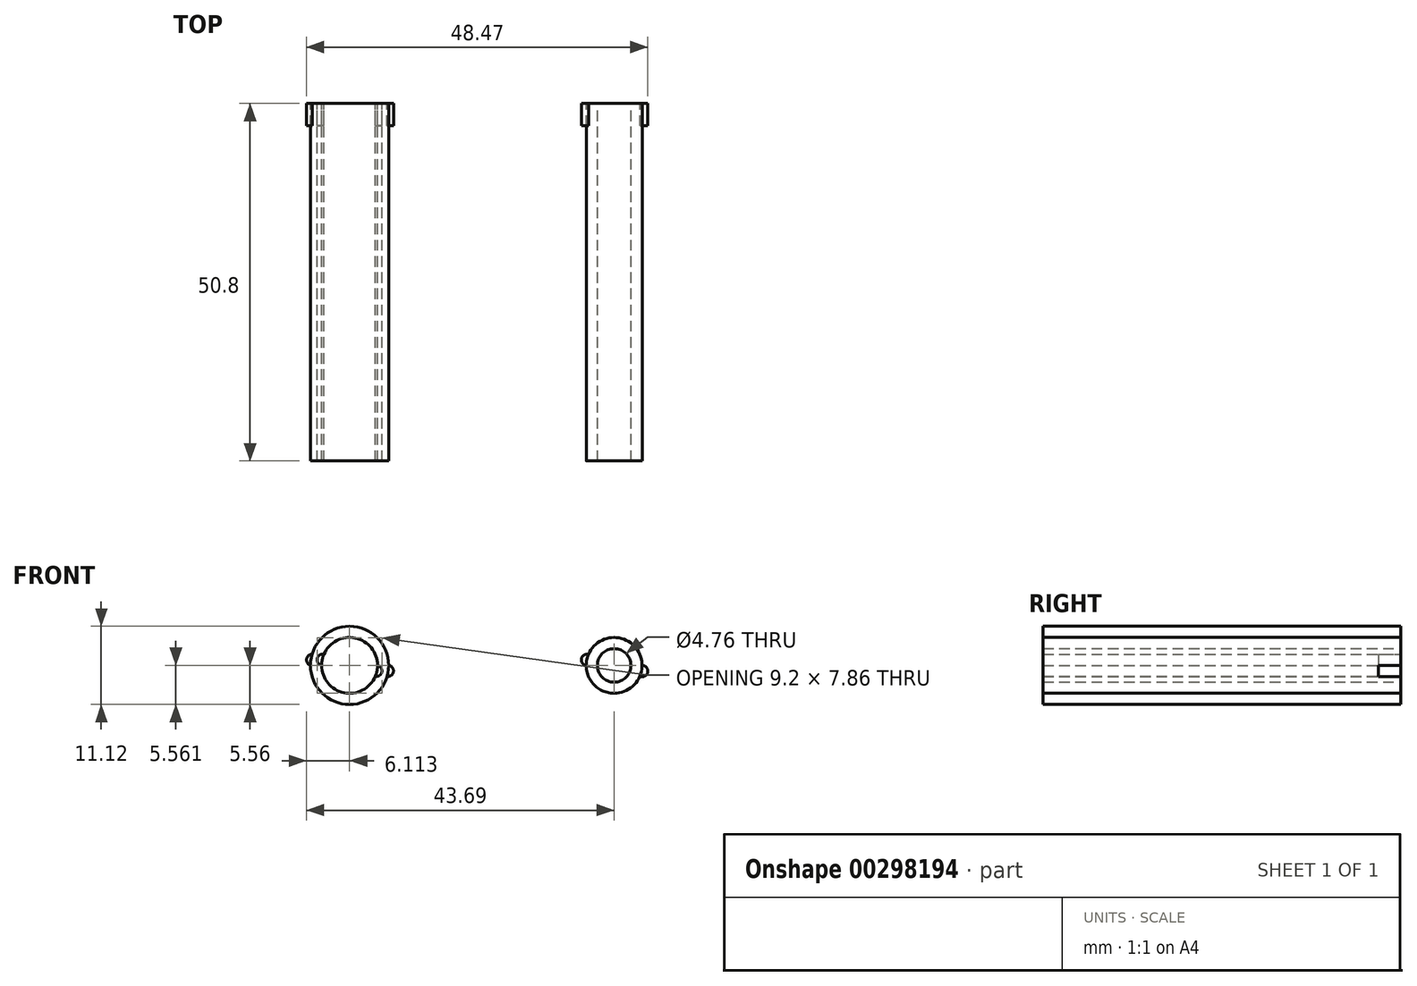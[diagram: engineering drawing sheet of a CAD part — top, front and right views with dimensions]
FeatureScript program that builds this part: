
annotation { "Feature Type Name" : "Feature", "Feature Type Description" : "" }
export const myFeature = defineFeature(function(context is Context, id is Id, definition is map)
    precondition{}
    {
        {
            var Q0;
            Q0=qCreatedBy(makeId("Front.planeOp"),FACE);
            var sketch = newSketch(context, id + "F0", { "sketchPlane" : qUnion([Q0])});
            skCircle(sketch, "E0", {"center": v(46.3, 0) * mm, "radius": 3.97 * mm});
            skCircle(sketch, "E1", {"center": v(8.73, 0) * mm, "radius": 5.56 * mm});
            skCircle(sketch, "E2.0", {"center": v(46.3, 0) * mm, "radius": 2.38 * mm});
            skCircle(sketch, "E3.0", {"center": v(8.73, 0) * mm, "radius": 3.97 * mm});
            skArc(sketch, "E4", {"start": v(3.4, 1.59) * mm, "mid": v(2.62, 0.9) * mm, "end": v(3.18, 0) * mm});
            skArc(sketch, "E5", {"start": v(14.06, -1.57) * mm, "mid": v(14.96, -0.9) * mm, "end": v(14.29, 0) * mm});
            skArc(sketch, "E6", {"start": v(5.1, 1.59) * mm, "mid": v(4.13, 0.96) * mm, "end": v(4.76, 0) * mm});
            skArc(sketch, "E7", {"start": v(12.38, -1.56) * mm, "mid": v(13.32, -0.94) * mm, "end": v(12.7, 0) * mm});
            skArc(sketch, "E8", {"start": v(42.65, 1.56) * mm, "mid": v(41.65, 0.95) * mm, "end": v(42.33, 0) * mm});
            skArc(sketch, "E9", {"start": v(49.95, -1.56) * mm, "mid": v(51.06, -0.97) * mm, "end": v(50.27, 0) * mm});
            skSolve(sketch);
        }
        {
            var Q0;
            Q0=makeQuery(id+"F0.imprint","IMPRINT",FACE,{"disambiguationData":[TD([[makeQuery(id+"F0.imprint","IMPRINT",EDGE,{"derivedFrom":sQuery(id+"F0.wireOp",EDGE,"E2.0")}),-1.0]])]});
            var Q1;
            {var subQ7=sQuery(id+"F0.wireOp",EDGE,"E6");Q1=makeQuery(id+"F0.imprint","IMPRINT",FACE,{"disambiguationData":[TD([[makeQuery(id+"F0.imprint","IMPRINT",EDGE,{"derivedFrom":subQ7}),-1.0]])]});}
            extrude(context, id + "F1", {"entities" : qUnion([Q0, Q1]), "depth" : 50.8 * mm});
        }
        {
            var Q0;
            {var subQ0=sQuery(id+"F0.wireOp",EDGE,"E6");Q0=makeQuery(id+"F0.imprint","IMPRINT",FACE,{"disambiguationData":[TD([[makeQuery(id+"F0.imprint","IMPRINT",EDGE,{"derivedFrom":subQ0}),1.0]])]});}
            var Q1;
            {var subQ0=sQuery(id+"F0.wireOp",EDGE,"E7");Q1=makeQuery(id+"F0.imprint","IMPRINT",FACE,{"disambiguationData":[TD([[makeQuery(id+"F0.imprint","IMPRINT",EDGE,{"derivedFrom":subQ0}),1.0]])]});}
            var Q2;
            {var subQ0=sQuery(id+"F0.wireOp",EDGE,"E5");Q2=makeQuery(id+"F0.imprint","IMPRINT",FACE,{"disambiguationData":[TD([[makeQuery(id+"F0.imprint","IMPRINT",EDGE,{"derivedFrom":subQ0}),1.0]])]});}
            var Q3;
            {var subQ0=sQuery(id+"F0.wireOp",EDGE,"E4");Q3=makeQuery(id+"F0.imprint","IMPRINT",FACE,{"disambiguationData":[TD([[makeQuery(id+"F0.imprint","IMPRINT",EDGE,{"derivedFrom":subQ0}),1.0]])]});}
            var Q4;
            {var subQ0=sQuery(id+"F0.wireOp",EDGE,"P9wS2eRt-gNgB-vEHD-qdaP-UL0ial1GIJOu");Q4=makeQuery(id+"F0.imprint","IMPRINT",FACE,{"disambiguationData":[TD([[makeQuery(id+"F0.imprint","IMPRINT",EDGE,{"derivedFrom":subQ0}),1.0]])]});}
            var Q5;
            {var subQ0=sQuery(id+"F0.wireOp",EDGE,"W7dkiZ6h-pHjP-ikNK-OOKP-RiI25K9TWIuu");Q5=makeQuery(id+"F0.imprint","IMPRINT",FACE,{"disambiguationData":[TD([[makeQuery(id+"F0.imprint","IMPRINT",EDGE,{"derivedFrom":subQ0}),1.0]])]});}
            extrude(context, id + "F2", {"entities" : qUnion([Q0, Q1, Q2, Q3, Q4, Q5]), "depth" : 3.17 * mm});
        }
        {
            var Q0;
            {var subQ0=sQuery(id+"F0.wireOp",EDGE,"E9");Q0=makeQuery(id+"F0.imprint","IMPRINT",FACE,{"disambiguationData":[TD([[makeQuery(id+"F0.imprint","IMPRINT",EDGE,{"derivedFrom":subQ0}),1.0]])]});}
            var Q1;
            {var subQ1=sQuery(id+"F0.wireOp",EDGE,"E8");Q1=makeQuery(id+"F0.imprint","IMPRINT",FACE,{"disambiguationData":[TD([[makeQuery(id+"F0.imprint","IMPRINT",EDGE,{"derivedFrom":subQ1}),1.0]])]});}
            extrude(context, id + "F3", {"entities" : qUnion([Q0, Q1]), "operationType" : NewBodyOperationType.ADD, "depth" : 3.17 * mm});
        }
    });
